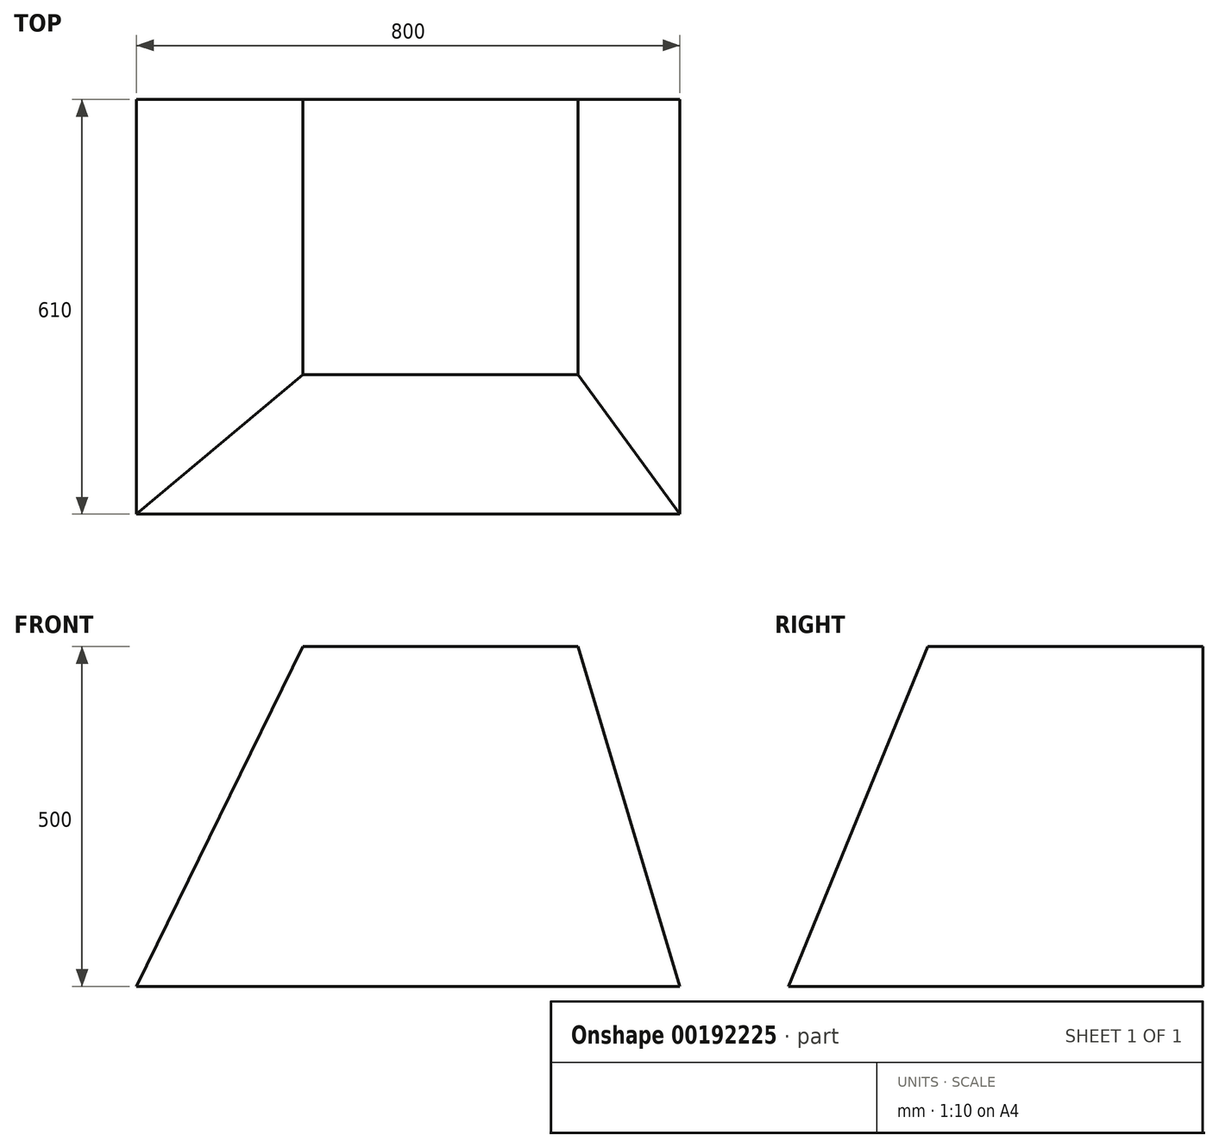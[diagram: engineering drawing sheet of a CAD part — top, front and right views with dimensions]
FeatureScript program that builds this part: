
annotation { "Feature Type Name" : "Feature", "Feature Type Description" : "" }
export const myFeature = defineFeature(function(context is Context, id is Id, definition is map)
    precondition{}
    {
        {
            var Q0;
            Q0=qCreatedBy(makeId("Top.planeOp"),FACE);
            var sketch = newSketch(context, id + "F0", { "sketchPlane" : qUnion([Q0])});
            skLineSegment(sketch, "E0.bottom", {"start": v(-400, 305) * mm, "end": v(400, 305) * mm});
            skLineSegment(sketch, "E0.top", {"start": v(-400, -305) * mm, "end": v(400, -305) * mm});
            skLineSegment(sketch, "E0.left", {"start": v(-400, 305) * mm, "end": v(-400, -305) * mm});
            skLineSegment(sketch, "E0.right", {"start": v(400, 305) * mm, "end": v(400, -305) * mm});
            skSolve(sketch);
        }
        {
            var Q0;
            Q0=makeQuery(id+"F0.imprint","IMPRINT",FACE,{"disambiguationData":[TD([[makeQuery(id+"F0.imprint","IMPRINT",EDGE,{"derivedFrom":sQuery(id+"F0.wireOp",EDGE,"E0.bottom")}),-1.0]])]});
            extrude(context, id + "F1", {"entities" : qUnion([Q0]), "endBound" : BoundingType.SYMMETRIC, "depth" : 500 * mm});
        }
        {
            var Q0;
            Q0=makeQuery(id+"F1.opExtrude","SWEPT_FACE",FACE,{"disambiguationData":[OSD([sQuery(id+"F0.wireOp",EDGE,"E0.top")])]});
            var sketch = newSketch(context, id + "F2", { "sketchPlane" : qUnion([Q0])});
            skLineSegment(sketch, "E1.0", {"start": v(-400, 250) * mm, "end": v(400, 250) * mm});
            skLineSegment(sketch, "E2.0", {"start": v(-400, 250) * mm, "end": v(-400, -250) * mm});
            skLineSegment(sketch, "E3.0", {"start": v(-400, -250) * mm, "end": v(400, -250) * mm});
            skLineSegment(sketch, "E4.0", {"start": v(400, 250) * mm, "end": v(400, -250) * mm});
            skLineSegment(sketch, "E5", {"start": v(-155, 250) * mm, "end": v(-400, -250) * mm});
            skLineSegment(sketch, "E6", {"start": v(-400, -250) * mm, "end": v(-400, 250) * mm});
            skLineSegment(sketch, "E7", {"start": v(-400, 250) * mm, "end": v(-155, 250) * mm});
            skLineSegment(sketch, "E8", {"start": v(250, 250) * mm, "end": v(400, -250) * mm});
            skLineSegment(sketch, "E9", {"start": v(400, -250) * mm, "end": v(400, 250) * mm});
            skLineSegment(sketch, "E10", {"start": v(400, 250) * mm, "end": v(250, 250) * mm});
            skSolve(sketch);
        }
        {
            var Q0;
            Q0=makeQuery(id+"F2.imprint","IMPRINT",FACE,{"disambiguationData":[TD([[makeQuery(id+"F2.imprint","IMPRINT",EDGE,{"derivedFrom":sQuery(id+"F2.wireOp",EDGE,"E5")}),-1.0]])]});
            var Q1;
            Q1=makeQuery(id+"F2.imprint","IMPRINT",FACE,{"disambiguationData":[TD([[makeQuery(id+"F2.imprint","IMPRINT",EDGE,{"derivedFrom":sQuery(id+"F2.wireOp",EDGE,"E8")}),1.0]])]});
            extrude(context, id + "F3", {"entities" : qUnion([Q0, Q1]), "operationType" : NewBodyOperationType.REMOVE, "endBound" : BoundingType.THROUGH_ALL, "oppositeDirection" : true, "depth" : 25 * mm});
        }
        {
            var Q0;
            Q0=qCreatedBy(makeId("Right.planeOp"),FACE);
            cPlane(context, id + "F4", {"entities" : qUnion([Q0]), "cplaneType" : CPlaneType.OFFSET, "offset" : 400 * mm, "oppositeDirection" : true, "width" : 150 * mm, "height" : 150 * mm});
        }
        {
            var Q0;
            Q0=qCreatedBy(id+"F4.planeOp",FACE);
            var sketch = newSketch(context, id + "F5", { "sketchPlane" : qUnion([Q0])});
            skLineSegment(sketch, "E11.0", {"start": v(305, 250) * mm, "end": v(-305, 250) * mm});
            skLineSegment(sketch, "E12.0", {"start": v(305, -250) * mm, "end": v(305, 250) * mm});
            skLineSegment(sketch, "E13.0", {"start": v(-305, 250) * mm, "end": v(-305, -250) * mm});
            skLineSegment(sketch, "E14.0", {"start": v(305, -250) * mm, "end": v(-305, -250) * mm});
            skLineSegment(sketch, "E15", {"start": v(305, 250) * mm, "end": v(305, -250) * mm});
            skLineSegment(sketch, "E16", {"start": v(305, 250) * mm, "end": v(305, 250) * mm});
            skLineSegment(sketch, "E17", {"start": v(-100, 250) * mm, "end": v(-305, -250) * mm});
            skLineSegment(sketch, "E18", {"start": v(-305, -250) * mm, "end": v(-305, 250) * mm});
            skLineSegment(sketch, "E19", {"start": v(-305, 250) * mm, "end": v(-100, 250) * mm});
            skSolve(sketch);
        }
        {
            var Q0;
            Q0=makeQuery(id+"F5.imprint","IMPRINT",FACE,{"disambiguationData":[TD([[makeQuery(id+"F5.imprint","IMPRINT",EDGE,{"derivedFrom":sQuery(id+"F5.wireOp",EDGE,"E17")}),-1.0]])]});
            extrude(context, id + "F6", {"entities" : qUnion([Q0]), "operationType" : NewBodyOperationType.REMOVE, "endBound" : BoundingType.THROUGH_ALL, "depth" : 25 * mm});
        }
    });
